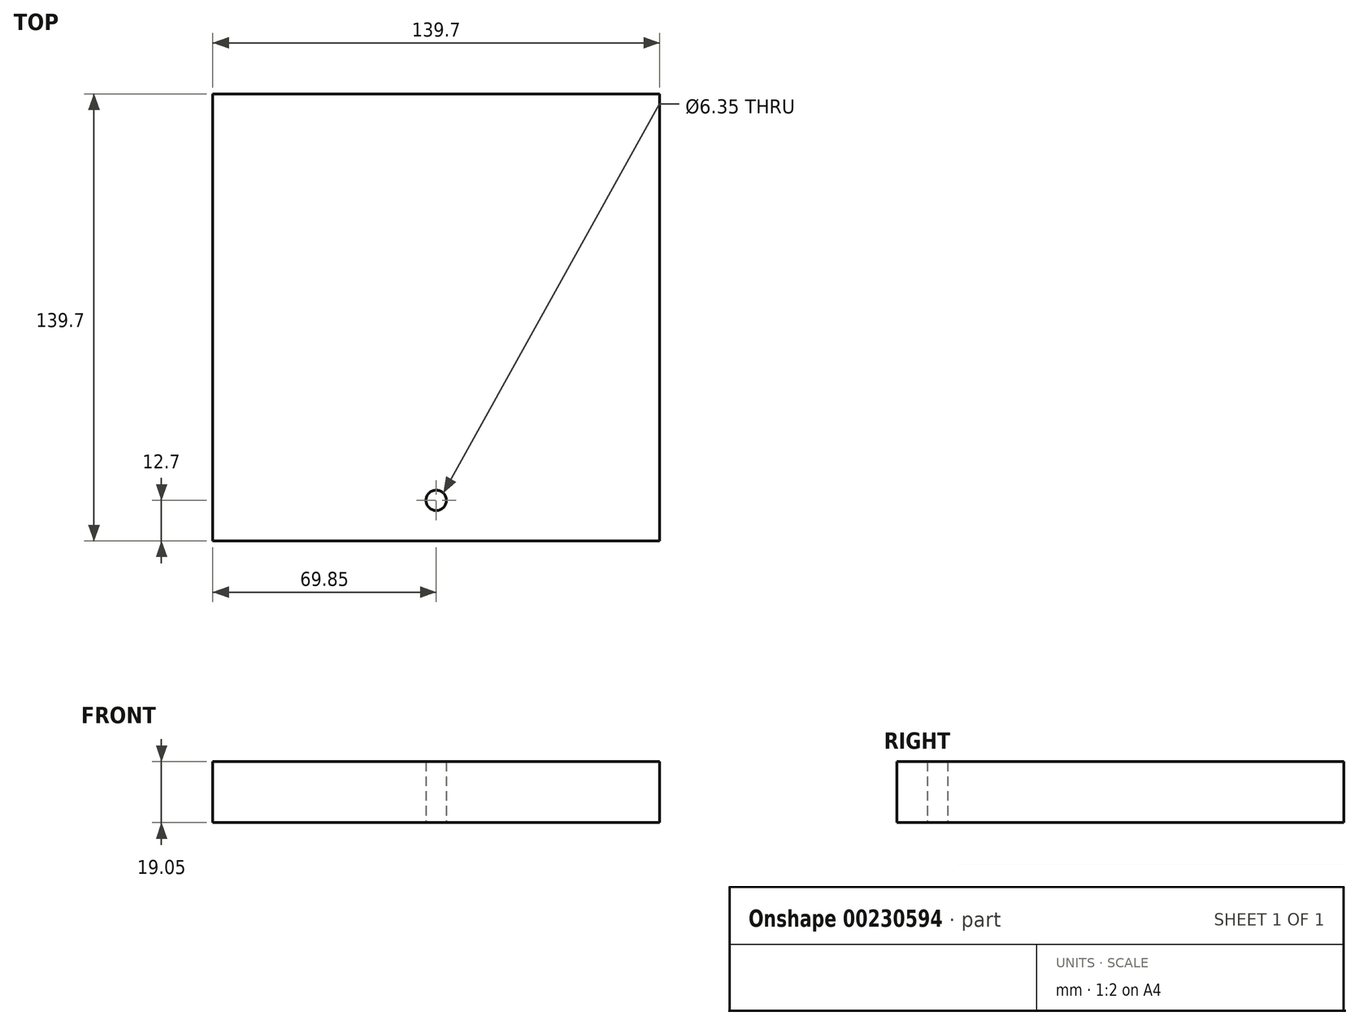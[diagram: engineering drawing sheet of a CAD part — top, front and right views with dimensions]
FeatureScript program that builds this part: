
annotation { "Feature Type Name" : "Feature", "Feature Type Description" : "" }
export const myFeature = defineFeature(function(context is Context, id is Id, definition is map)
    precondition{}
    {
        {
            var Q0;
            Q0=qCreatedBy(makeId("Top.planeOp"),FACE);
            var sketch = newSketch(context, id + "F0", { "sketchPlane" : qUnion([Q0])});
            skLineSegment(sketch, "E0.bottom", {"start": v(69.85, 69.85) * mm, "end": v(-69.85, 69.85) * mm});
            skLineSegment(sketch, "E0.top", {"start": v(69.85, -69.85) * mm, "end": v(-69.85, -69.85) * mm});
            skLineSegment(sketch, "E0.left", {"start": v(69.85, 69.85) * mm, "end": v(69.85, -69.85) * mm});
            skLineSegment(sketch, "E0.right", {"start": v(-69.85, 69.85) * mm, "end": v(-69.85, -69.85) * mm});
            skPoint(sketch, "E0.middle", {"position": v(0, 0) * mm});
            skLineSegment(sketch, "E1", {"start": v(0, -69.85) * mm, "end": v(0, -57.15) * mm});
            skPoint(sketch, "E1.endSnap0", {"position": v(0, -69.85) * mm});
            skCircle(sketch, "E2", {"center": v(0, -57.15) * mm, "radius": 3.18 * mm});
            skSolve(sketch);
        }
        {
            var Q0;
            Q0 = qSketchRegion(id + "F0", true);
            extrude(context, id + "F1", {"entities" : qUnion([Q0]), "depth" : 19.05 * mm});
        }
    });
